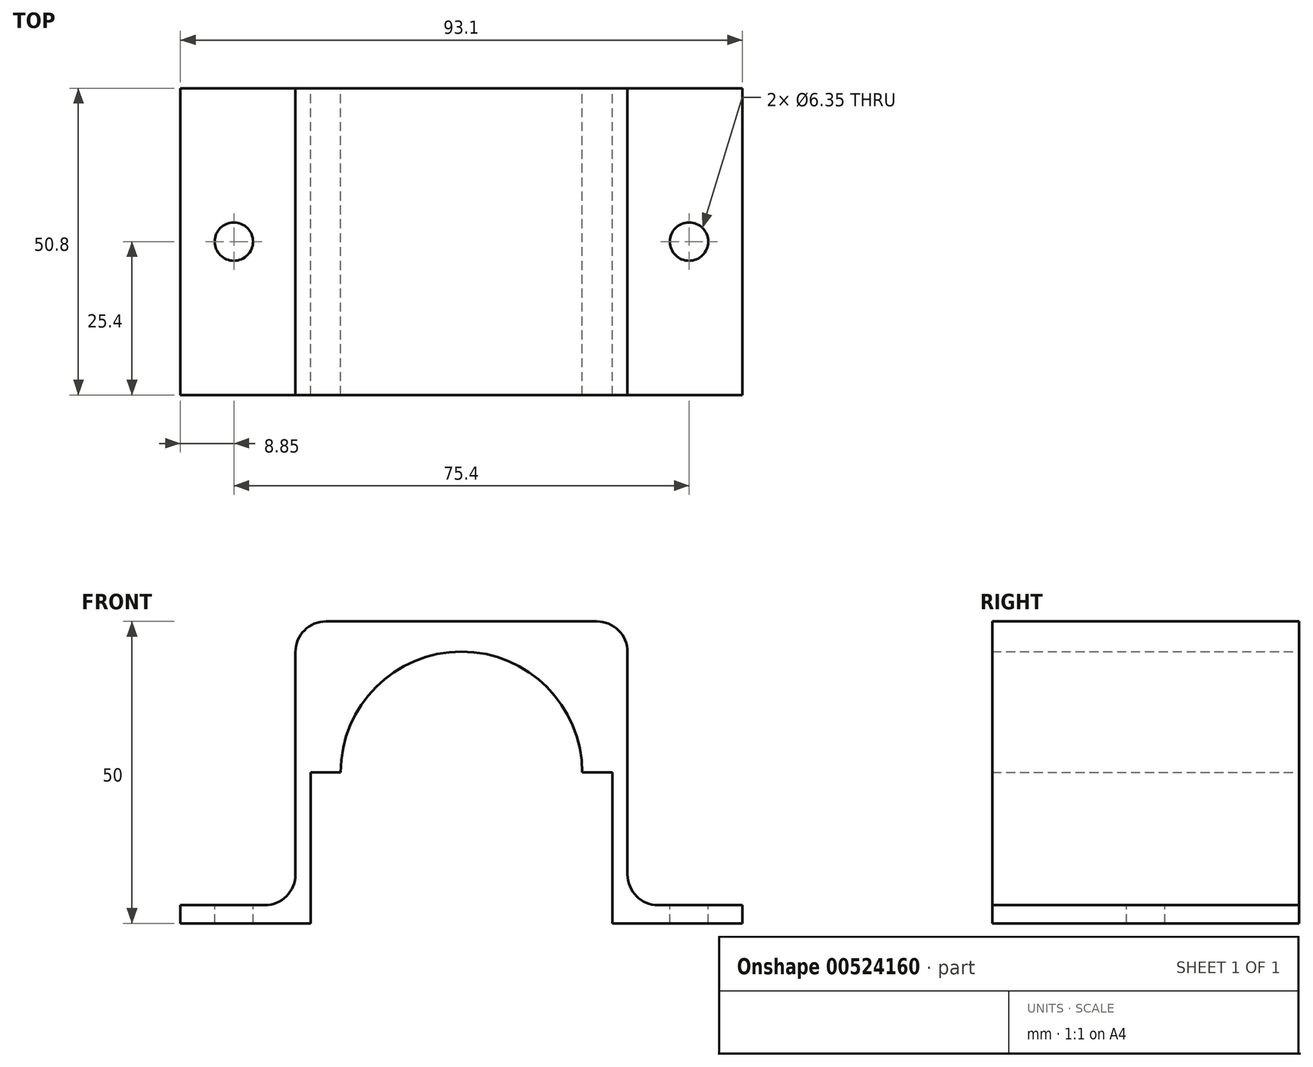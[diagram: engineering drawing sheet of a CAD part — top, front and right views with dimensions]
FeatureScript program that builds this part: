
annotation { "Feature Type Name" : "Feature", "Feature Type Description" : "" }
export const myFeature = defineFeature(function(context is Context, id is Id, definition is map)
    precondition{}
    {
        {
            var Q0;
            Q0=qCreatedBy(makeId("Front.planeOp"),FACE);
            var sketch = newSketch(context, id + "F0", { "sketchPlane" : qUnion([Q0])});
            skLineSegment(sketch, "E0.bottom", {"start": v(-25, 0) * mm, "end": v(-20, 0) * mm});
            skLineSegment(sketch, "E0.top", {"start": v(-27.5, 25) * mm, "end": v(27.5, 25) * mm});
            skLineSegment(sketch, "E0.left", {"start": v(-27.5, 0) * mm, "end": v(-27.5, 25) * mm});
            skLineSegment(sketch, "E0.right", {"start": v(27.5, 0) * mm, "end": v(27.5, 25) * mm});
            skArc(sketch, "E1", {"start": v(20, 0) * mm, "mid": v(0, 20) * mm, "end": v(-20, 0) * mm});
            skLineSegment(sketch, "E2.trimOffspring", {"start": v(20, 0) * mm, "end": v(25, 0) * mm});
            skLineSegment(sketch, "E3", {"start": v(-25, 0) * mm, "end": v(-25, -25) * mm});
            skLineSegment(sketch, "E4", {"start": v(-25, -25) * mm, "end": v(-46.55, -25) * mm});
            skLineSegment(sketch, "E5", {"start": v(25, 0) * mm, "end": v(25, -25) * mm});
            skLineSegment(sketch, "E6", {"start": v(-27.5, 0) * mm, "end": v(-27.5, -22) * mm});
            skLineSegment(sketch, "E7", {"start": v(-27.5, -22) * mm, "end": v(-46.55, -22) * mm});
            skLineSegment(sketch, "E8", {"start": v(-46.55, -22) * mm, "end": v(-46.55, -25) * mm});
            skLineSegment(sketch, "E9", {"start": v(25, -25) * mm, "end": v(46.55, -25) * mm});
            skLineSegment(sketch, "E10", {"start": v(46.55, -25) * mm, "end": v(46.55, -22) * mm});
            skLineSegment(sketch, "E11", {"start": v(46.55, -22) * mm, "end": v(27.5, -22) * mm});
            skLineSegment(sketch, "E12", {"start": v(27.5, -22) * mm, "end": v(27.5, 0) * mm});
            skSolve(sketch);
        }
        {
            var Q0;
            Q0=makeQuery(id+"F0.imprint","IMPRINT",FACE,{"disambiguationData":[TD([[makeQuery(id+"F0.imprint","IMPRINT",EDGE,{"derivedFrom":sQuery(id+"F0.wireOp",EDGE,"E0.bottom")}),-1.0]])]});
            var Q1;
            Q1=makeQuery(id+"F0.imprint","IMPRINT",FACE,{"disambiguationData":[TD([[makeQuery(id+"F0.imprint","IMPRINT",EDGE,{"derivedFrom":sQuery(id+"F0.wireOp",EDGE,"E0.bottom")}),1.0]])]});
            var Q2;
            Q2=makeQuery(id+"F0.imprint","IMPRINT",FACE,{"disambiguationData":[TD([[makeQuery(id+"F0.imprint","IMPRINT",EDGE,{"derivedFrom":sQuery(id+"F0.wireOp",EDGE,"E2.trimOffspring")}),-1.0]])]});
            extrude(context, id + "F1", {"entities" : qUnion([Q0, Q1, Q2]), "depth" : 50.8 * mm});
        }
        {
            var Q0;
            Q0=makeQuery(id+"F1.opExtrude","SWEPT_EDGE",EDGE,{"disambiguationData":[OSD([sQuery(id+"F0.wireOp",EDGE,"E0.top"),sQuery(id+"F0.wireOp",EDGE,"E0.left")])]});
            var Q1;
            Q1=makeQuery(id+"F1.opExtrude","SWEPT_EDGE",EDGE,{"disambiguationData":[OSD([sQuery(id+"F0.wireOp",EDGE,"E0.top"),sQuery(id+"F0.wireOp",EDGE,"E0.right")])]});
            fillet(context, id + "F2", {"entities" : qUnion([Q0, Q1]), "radius" : 5.08 * mm, "tangentPropagation" : true, "allowEdgeOverflow" : false});
        }
        {
            var Q0;
            Q0=makeQuery(id+"F1.opExtrude","SWEPT_EDGE",EDGE,{"disambiguationData":[OSD([sQuery(id+"F0.wireOp",EDGE,"E6"),sQuery(id+"F0.wireOp",EDGE,"E7")])]});
            var Q1;
            Q1=makeQuery(id+"F1.opExtrude","SWEPT_EDGE",EDGE,{"disambiguationData":[OSD([sQuery(id+"F0.wireOp",EDGE,"E11"),sQuery(id+"F0.wireOp",EDGE,"E12")])]});
            fillet(context, id + "F3", {"entities" : qUnion([Q0, Q1]), "radius" : 5.08 * mm, "tangentPropagation" : true, "allowEdgeOverflow" : false});
        }
        {
            var Q0;
            Q0=makeQuery(id+"F1.opExtrude","SWEPT_FACE",FACE,{"disambiguationData":[OSD([sQuery(id+"F0.wireOp",EDGE,"E7")])]});
            var sketch = newSketch(context, id + "F4", { "sketchPlane" : qUnion([Q0])});
            skCircle(sketch, "E13", {"center": v(-37.7, -25.4) * mm, "radius": 3.18 * mm});
            skPoint(sketch, "E13.centerSnap0", {"position": v(-25, -25.4) * mm});
            skCircle(sketch, "E14", {"center": v(37.7, -25.4) * mm, "radius": 3.18 * mm});
            skSolve(sketch);
        }
        {
            var Q0;
            Q0=qSketchRegion(id+"F4",true);
            extrude(context, id + "F5", {"entities" : qUnion([Q0]), "operationType" : NewBodyOperationType.REMOVE, "oppositeDirection" : true, "depth" : 25.4 * mm});
        }
    });
